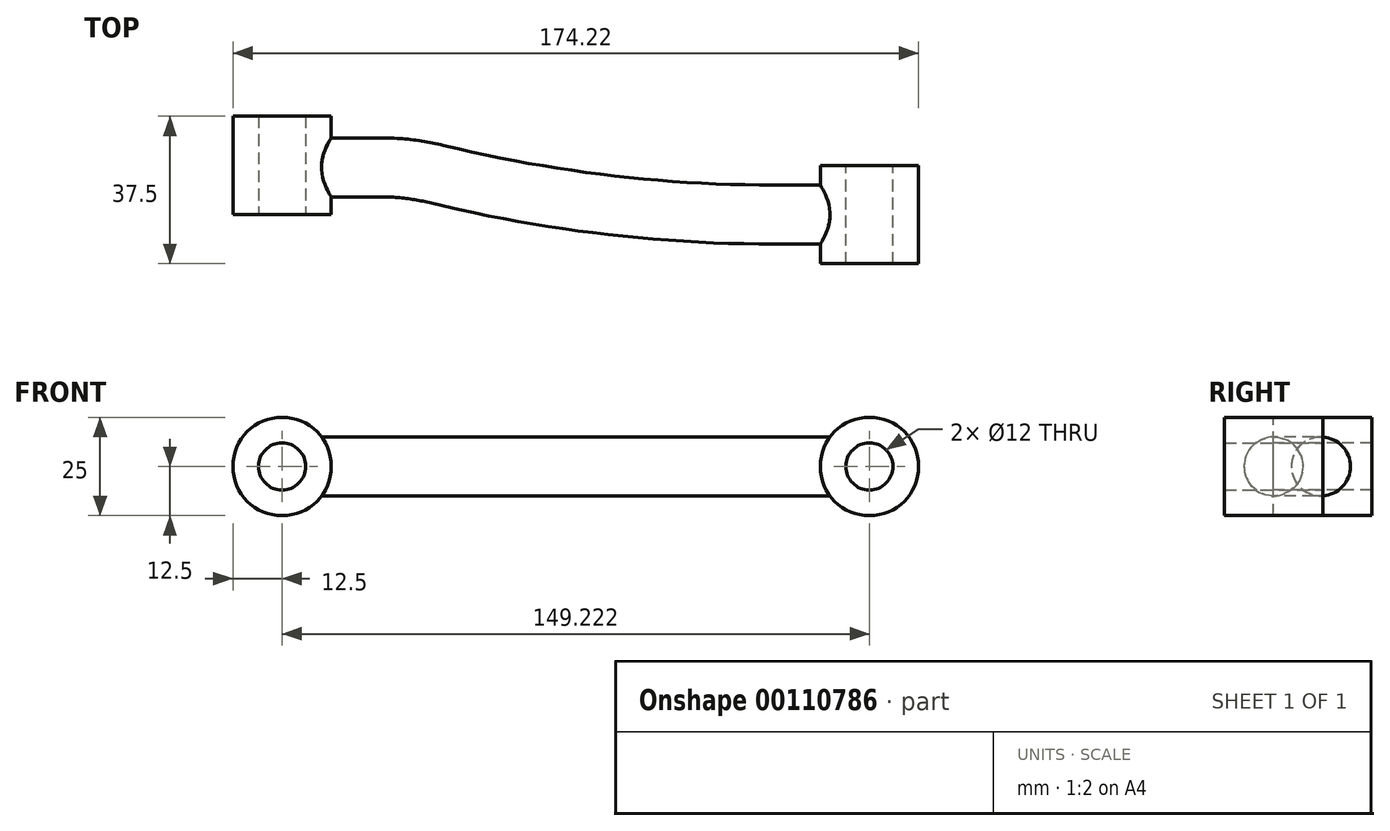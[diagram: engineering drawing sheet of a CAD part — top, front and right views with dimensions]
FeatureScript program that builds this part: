
annotation { "Feature Type Name" : "Feature", "Feature Type Description" : "" }
export const myFeature = defineFeature(function(context is Context, id is Id, definition is map)
    precondition{}
    {
        {
            var Q0;
            Q0=qCreatedBy(makeId("Top.planeOp"),FACE);
            var sketch = newSketch(context, id + "F0", { "sketchPlane" : qUnion([Q0])});
            skLineSegment(sketch, "E0", {"start": v(0, 0) * mm, "end": v(25, 0) * mm});
            skLineSegment(sketch, "E1", {"start": v(125, -12) * mm, "end": v(150, -12) * mm});
            skArc(sketch, "E2", {"start": v(25, 0) * mm, "mid": v(32.15, -0.43) * mm, "end": v(39.2, -1.7) * mm});
            skArc(sketch, "E3", {"start": v(39.2, -1.7) * mm, "mid": v(81.79, -9.42) * mm, "end": v(125, -12) * mm});
            skSolve(sketch);
        }
        {
            var Q0;
            Q0=qCreatedBy(makeId("Front.planeOp"),FACE);
            var sketch = newSketch(context, id + "F1", { "sketchPlane" : qUnion([Q0])});
            skCircle(sketch, "E4", {"center": v(0, 0) * mm, "radius": 6 * mm});
            skCircle(sketch, "E5", {"center": v(0, 0) * mm, "radius": 12.5 * mm});
            skSolve(sketch);
        }
        {
            var Q0;
            Q0=makeQuery(id+"F1.imprint","IMPRINT",FACE,{"disambiguationData":[TD([[makeQuery(id+"F1.imprint","IMPRINT",EDGE,{"derivedFrom":sQuery(id+"F1.wireOp",EDGE,"E4")}),-1.0]])]});
            extrude(context, id + "F2", {"entities" : qUnion([Q0]), "oppositeDirection" : true, "depth" : 13 * mm});
        }
        {
            var Q0;
            Q0=makeQuery(id+"F2.opExtrude","CAP_FACE",FACE,{"disambiguationData":[OSD([sQuery(id+"F1.wireOp",EDGE,"E4"),sQuery(id+"F1.wireOp",EDGE,"E5")])],"isStart":true});
            extrude(context, id + "F3", {"entities" : qUnion([Q0]), "operationType" : NewBodyOperationType.ADD, "depth" : 12 * mm});
        }
        {
            var Q0;
            Q0=qCreatedBy(makeId("Right.planeOp"),FACE);
            var sketch = newSketch(context, id + "F4", { "sketchPlane" : qUnion([Q0])});
            skCircle(sketch, "E6", {"center": v(0, 0) * mm, "radius": 7.5 * mm});
            skSolve(sketch);
        }
        {
            var Q0;
            Q0=makeQuery(id+"F4.imprint","IMPRINT",FACE,{"disambiguationData":[TD([[makeQuery(id+"F4.imprint","IMPRINT",EDGE,{"derivedFrom":sQuery(id+"F4.wireOp",EDGE,"E6")}),1.0]])]});
            var Q1;
            Q1=sQuery(id+"F0.wireOp",EDGE,"E0");
            var Q2;
            Q2=sQuery(id+"F0.wireOp",EDGE,"E2");
            var Q3;
            Q3=sQuery(id+"F0.wireOp",EDGE,"E3");
            var Q4;
            Q4=sQuery(id+"F0.wireOp",EDGE,"E1");
            sweep(context, id + "F5", {"operationType" : NewBodyOperationType.ADD, "profiles" : qUnion([Q0]), "path" : qUnion([Q1, Q2, Q3, Q4])});
        }
        {
            var Q0;
            Q0=makeQuery(id+"F2.opExtrude","CAP_FACE",FACE,{"disambiguationData":[OSD([sQuery(id+"F1.wireOp",EDGE,"E4"),sQuery(id+"F1.wireOp",EDGE,"E5")])],"isStart":false});
            var sketch = newSketch(context, id + "F6", { "sketchPlane" : qUnion([Q0])});
            skSolve(sketch);
        }
        {
            var Q0;
            Q0 = qSketchRegion(id + "F6", true);
            var Q1;
            Q1=makeQuery(id+"F6.imprint","IMPRINT",FACE,{"disambiguationData":[TD([[makeQuery(id+"F6.imprint","IMPRINT",EDGE,{"derivedFrom":makeQuery(id+"F2.opExtrude","CAP_EDGE",EDGE,{"disambiguationData":[OSD([sQuery(id+"F1.wireOp",EDGE,"E4")])],"isStart":false})}),-1.0]])]});
            extrude(context, id + "F7", {"entities" : qUnion([Q0, Q1]), "operationType" : NewBodyOperationType.REMOVE, "endBound" : BoundingType.THROUGH_ALL, "oppositeDirection" : true, "depth" : 25 * mm});
        }
        {
            var Q0;
            Q0=makeQuery(id+"F3.opExtrude","CAP_FACE",FACE,{"disambiguationData":[OSD([sQuery(id+"F1.wireOp",EDGE,"E4"),sQuery(id+"F1.wireOp",EDGE,"E5")])],"isStart":false});
            var sketch = newSketch(context, id + "F8", { "sketchPlane" : qUnion([Q0])});
            skCircle(sketch, "E7", {"center": v(149.22, 0) * mm, "radius": 6 * mm});
            skCircle(sketch, "E8", {"center": v(149.22, 0) * mm, "radius": 12.5 * mm});
            skSolve(sketch);
        }
        {
            var Q0;
            Q0 = qSketchRegion(id + "F8", true);
            extrude(context, id + "F9", {"entities" : qUnion([Q0]), "operationType" : NewBodyOperationType.ADD, "endBound" : BoundingType.SYMMETRIC, "depth" : 25 * mm});
        }
        {
            var Q0;
            Q0=makeQuery(id+"F9.opExtrude","CAP_FACE",FACE,{"disambiguationData":[OSD([sQuery(id+"F8.wireOp",EDGE,"E7"),sQuery(id+"F8.wireOp",EDGE,"E8")])],"isStart":false});
            var sketch = newSketch(context, id + "F10", { "sketchPlane" : qUnion([Q0])});
            skSolve(sketch);
        }
        {
            var Q0;
            Q0=makeQuery(id+"F10.imprint","IMPRINT",FACE,{"disambiguationData":[TD([[makeQuery(id+"F10.imprint","IMPRINT",EDGE,{"derivedFrom":makeQuery(id+"F9.opExtrude","CAP_EDGE",EDGE,{"disambiguationData":[OSD([sQuery(id+"F8.wireOp",EDGE,"E7")])],"isStart":false})}),1.0]])]});
            extrude(context, id + "F11", {"entities" : qUnion([Q0]), "operationType" : NewBodyOperationType.REMOVE, "endBound" : BoundingType.THROUGH_ALL, "oppositeDirection" : true, "depth" : 25 * mm});
        }
    });
